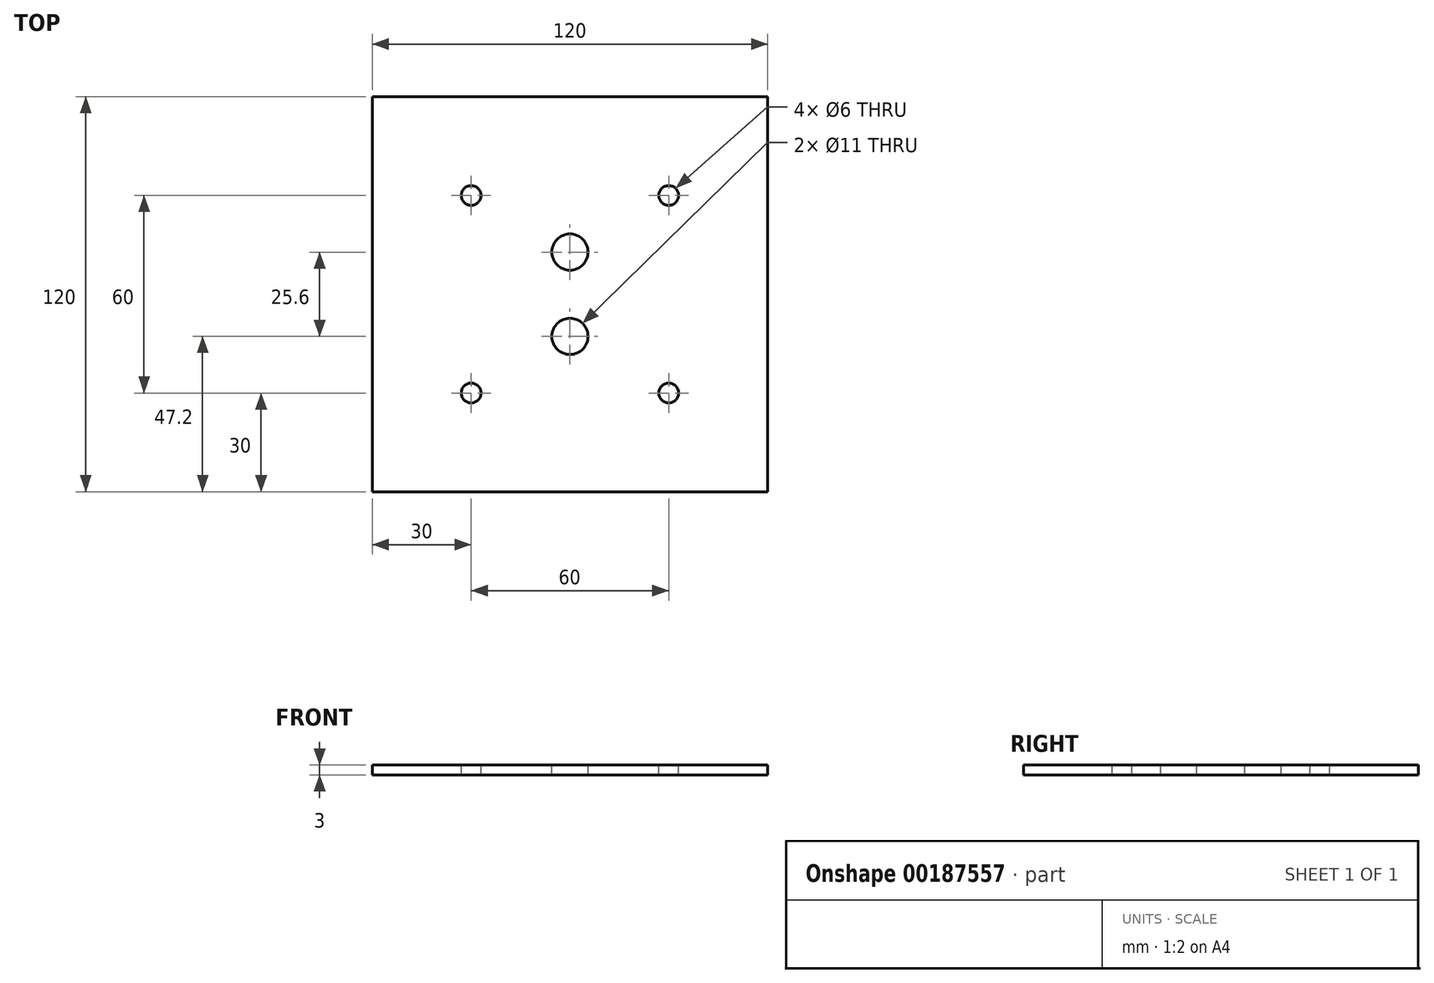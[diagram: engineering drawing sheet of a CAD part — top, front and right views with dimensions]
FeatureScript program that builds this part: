
annotation { "Feature Type Name" : "Feature", "Feature Type Description" : "" }
export const myFeature = defineFeature(function(context is Context, id is Id, definition is map)
    precondition{}
    {
        {
            var Q0;
            Q0=qCreatedBy(makeId("Top.planeOp"),FACE);
            var sketch = newSketch(context, id + "F0", { "sketchPlane" : qUnion([Q0])});
            skLineSegment(sketch, "E0.bottom", {"start": v(60, 60) * mm, "end": v(-60, 60) * mm});
            skLineSegment(sketch, "E0.top", {"start": v(60, -60) * mm, "end": v(-60, -60) * mm});
            skLineSegment(sketch, "E0.left", {"start": v(60, 60) * mm, "end": v(60, -60) * mm});
            skLineSegment(sketch, "E0.right", {"start": v(-60, 60) * mm, "end": v(-60, -60) * mm});
            skPoint(sketch, "E0.middle", {"position": v(0, 0) * mm});
            skSolve(sketch);
        }
        {
            var Q0;
            Q0=makeQuery(id+"F0.imprint","IMPRINT",FACE,{"disambiguationData":[TD([[makeQuery(id+"F0.imprint","IMPRINT",EDGE,{"derivedFrom":sQuery(id+"F0.wireOp",EDGE,"E0.bottom")}),1.0]])]});
            extrude(context, id + "F1", {"entities" : qUnion([Q0]), "depth" : 3 * mm});
        }
        {
            var Q0;
            Q0=makeQuery(id+"F1.opExtrude","CAP_FACE",FACE,{"disambiguationData":[OSD([sQuery(id+"F0.wireOp",EDGE,"E0.bottom"),sQuery(id+"F0.wireOp",EDGE,"E0.top"),sQuery(id+"F0.wireOp",EDGE,"E0.left"),sQuery(id+"F0.wireOp",EDGE,"E0.right")])],"isStart":false});
            var sketch = newSketch(context, id + "F2", { "sketchPlane" : qUnion([Q0])});
            skLineSegment(sketch, "E1", {"start": v(0, 60) * mm, "end": v(0, -60) * mm, "construction": true});
            skCircle(sketch, "E2", {"center": v(0, 12.8) * mm, "radius": 5.5 * mm});
            skCircle(sketch, "E3.MirrorC", {"center": v(0, -12.8) * mm, "radius": 5.5 * mm});
            skSolve(sketch);
        }
        {
            var Q0;
            Q0=qSketchRegion(id+"F2",true);
            extrude(context, id + "F3", {"entities" : qUnion([Q0]), "operationType" : NewBodyOperationType.REMOVE, "endBound" : BoundingType.THROUGH_ALL, "oppositeDirection" : true, "depth" : 25 * mm});
        }
        {
            var Q0;
            Q0=makeQuery(id+"F1.opExtrude","CAP_FACE",FACE,{"disambiguationData":[OSD([sQuery(id+"F0.wireOp",EDGE,"E0.bottom"),sQuery(id+"F0.wireOp",EDGE,"E0.top"),sQuery(id+"F0.wireOp",EDGE,"E0.left"),sQuery(id+"F0.wireOp",EDGE,"E0.right")])],"isStart":false});
            var sketch = newSketch(context, id + "F4", { "sketchPlane" : qUnion([Q0])});
            skLineSegment(sketch, "E4", {"start": v(-60, 0) * mm, "end": v(60, 0) * mm, "construction": true});
            skLineSegment(sketch, "E5.bottom", {"start": v(30, 30) * mm, "end": v(-30, 30) * mm, "construction": true});
            skLineSegment(sketch, "E5.top", {"start": v(30, -30) * mm, "end": v(-30, -30) * mm, "construction": true});
            skLineSegment(sketch, "E5.left", {"start": v(30, 30) * mm, "end": v(30, -30) * mm, "construction": true});
            skLineSegment(sketch, "E5.right", {"start": v(-30, 30) * mm, "end": v(-30, -30) * mm, "construction": true});
            skPoint(sketch, "E5.middle", {"position": v(0, 0) * mm});
            skCircle(sketch, "E6", {"center": v(-30, 30) * mm, "radius": 8.25 * mm, "construction": true});
            skCircle(sketch, "E7", {"center": v(30, 30) * mm, "radius": 8.25 * mm, "construction": true});
            skCircle(sketch, "E8", {"center": v(30, -30) * mm, "radius": 8.25 * mm, "construction": true});
            skCircle(sketch, "E9", {"center": v(-30, -30) * mm, "radius": 8.25 * mm, "construction": true});
            skCircle(sketch, "E10", {"center": v(30, 30) * mm, "radius": 8 * mm});
            skCircle(sketch, "E11", {"center": v(30, -30) * mm, "radius": 8 * mm});
            skCircle(sketch, "E12", {"center": v(-30, -30) * mm, "radius": 8 * mm});
            skCircle(sketch, "E13", {"center": v(-30, 30) * mm, "radius": 8 * mm});
            skSolve(sketch);
        }
        {
            var Q0;
            Q0=sQuery(id+"F4.wireOp",VERTEX,"E5.right.end");
            var Q1;
            Q1=sQuery(id+"F4.wireOp",VERTEX,"E13.center");
            var Q2;
            Q2=sQuery(id+"F4.wireOp",VERTEX,"E7.center");
            var Q3;
            Q3=sQuery(id+"F4.wireOp",VERTEX,"E5.left.end");
            var Q4;
            Q4=makeQuery(id+"F1.opExtrude","SWEPT_BODY",BODY,{"disambiguationData":[OSD([sQuery(id+"F0.wireOp",EDGE,"E0.bottom"),sQuery(id+"F0.wireOp",EDGE,"E0.top"),sQuery(id+"F0.wireOp",EDGE,"E0.left"),sQuery(id+"F0.wireOp",EDGE,"E0.right")])]});
            hole(context, id + "F5", {"style" : HoleStyle.SIMPLE, "endStyle" : HoleEndStyle.THROUGH, "holeDiameter" : 6 * mm, "locations" : qUnion([Q0, Q1, Q2, Q3]), "scope" : qUnion([Q4]), "isTappedThrough" : true});
        }
    });
